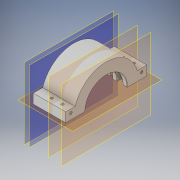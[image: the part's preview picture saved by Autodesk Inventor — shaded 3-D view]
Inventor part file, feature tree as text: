
AUTODESK INVENTOR PART (.ipt)
format: ipt  version: 2019 (Build 230136000, 136)  size: 546,816 bytes
history: native  units: mm
features: sketch x26, extrude x21, mirror x13, plane x12, projected_geometry x11, other x4, fillet x4, hole x3
ambient origin geometry x8: Origin, YZ Plane, XZ Plane, XY Plane, X Axis, Y Axis, Z Axis, Center Point
bodies: Body1 (feature_tree)
feature tree (94):
  other  "實體1"
  extrude  "擠出1"  Depth=123.43mm
  plane  "工作平面2"
  extrude  "擠出3"  Depth=160.0mm
  plane  "工作平面3"
  extrude  "擠出4"  Depth=120.0mm TaperAngle=0.0deg
  extrude  "擠出5"  [1 undecoded]
  plane  "工作平面4"
  extrude  "擠出7"  Depth=130.0mm
  plane  "工作平面5"
  extrude  "擠出9"  Depth=15.0mm TaperAngle=0.0deg
  extrude  "擠出10"  [1 undecoded]
  extrude  "擠出11"  Depth=140.0mm
  extrude  "擠出12"  Depth=10.0mm TaperAngle=0.0deg
  mirror  "鏡射1"
  fillet  "圓角2"  Radius=10.0mm
  fillet  "圓角3"  Radius=10.0mm
  sketch  "草圖16"
  plane  "工作平面7"
  mirror  "鏡射2"
  fillet  "圓角5"  [1 undecoded]
  fillet  "圓角6"  Radius=10.0mm
  plane  "工作平面8"
  plane  "工作平面9"
  sketch  "草圖20"
  extrude  "擠出15"  [1 undecoded]
  plane  "工作平面10"
  extrude  "擠出16"  Depth=10.0mm
  extrude  "擠出17"  Depth=10.0mm TaperAngle=0.0deg
  plane  "工作平面11"
  extrude  "擠出19"  Depth=10.0mm TaperAngle=0.0deg
  extrude  "擠出20"  Depth=160.0mm
  mirror  "鏡射3"
  mirror  "鏡射4"
  extrude  "擠出21"  Depth=80.0mm
  mirror  "鏡射7"
  plane  "工作平面15"
  mirror  "鏡射9"
  hole  "孔2"  [1 undecoded]
  mirror  "鏡射10"
  mirror  "鏡射11"
  hole  "孔3"  [1 undecoded]
  mirror  "鏡射12"
  mirror  "鏡射13"
  extrude  "擠出22"  Depth=160.0mm
  extrude  "擠出23"  Depth=120.0mm TaperAngle=0.0deg
  extrude  "擠出24"  Depth=120.0mm TaperAngle=0.0deg
  extrude  "擠出25"  Depth=25.0mm
  extrude  "擠出27"  Depth=20.0mm
  extrude  "擠出28"  Depth=2.0mm
  mirror  "鏡射14"
  plane  "工作平面17"
  hole  "孔4"  [1 undecoded]
  mirror  "鏡射15"
  mirror  "鏡射16"
  other  "分割2"
  other  "分割3"
  other  "分割4"
  sketch  "草圖1"
  sketch  "草圖4"
  sketch  "草圖6"
  sketch  "草圖7"
  projected_geometry  "投影迴路1"
  sketch  "草圖9"
  projected_geometry  "投影迴路4"
  sketch  "草圖11"
  sketch  "草圖12"
  projected_geometry  "投影迴路6"
  sketch  "草圖13"
  projected_geometry  "投影迴路7"
  sketch  "草圖14"
  plane  "工作平面6"
  sketch  "草圖17"
  projected_geometry  "投影迴路8"
  sketch  "草圖24"
  projected_geometry  "投影迴路11"
  sketch  "草圖25"
  sketch  "草圖26"
  sketch  "草圖27"
  sketch  "草圖28"
  sketch  "草圖29"
  projected_geometry  "投影迴路12"
  sketch  "草圖30"
  sketch  "草圖31"
  sketch  "草圖32"
  projected_geometry  "投影迴路13"
  projected_geometry  "投影迴路14"
  projected_geometry  "投影迴路15"
  sketch  "草圖33"
  sketch  "草圖34"
  sketch  "草圖35"
  projected_geometry  "投影迴路16"
  sketch  "草圖36"
  sketch  "草圖37"
note: 7 required parameter values undecoded (feature->parameter linkage not recoverable at this tier; creation-order binding heuristic only, values carry confidence <= 0.55)
